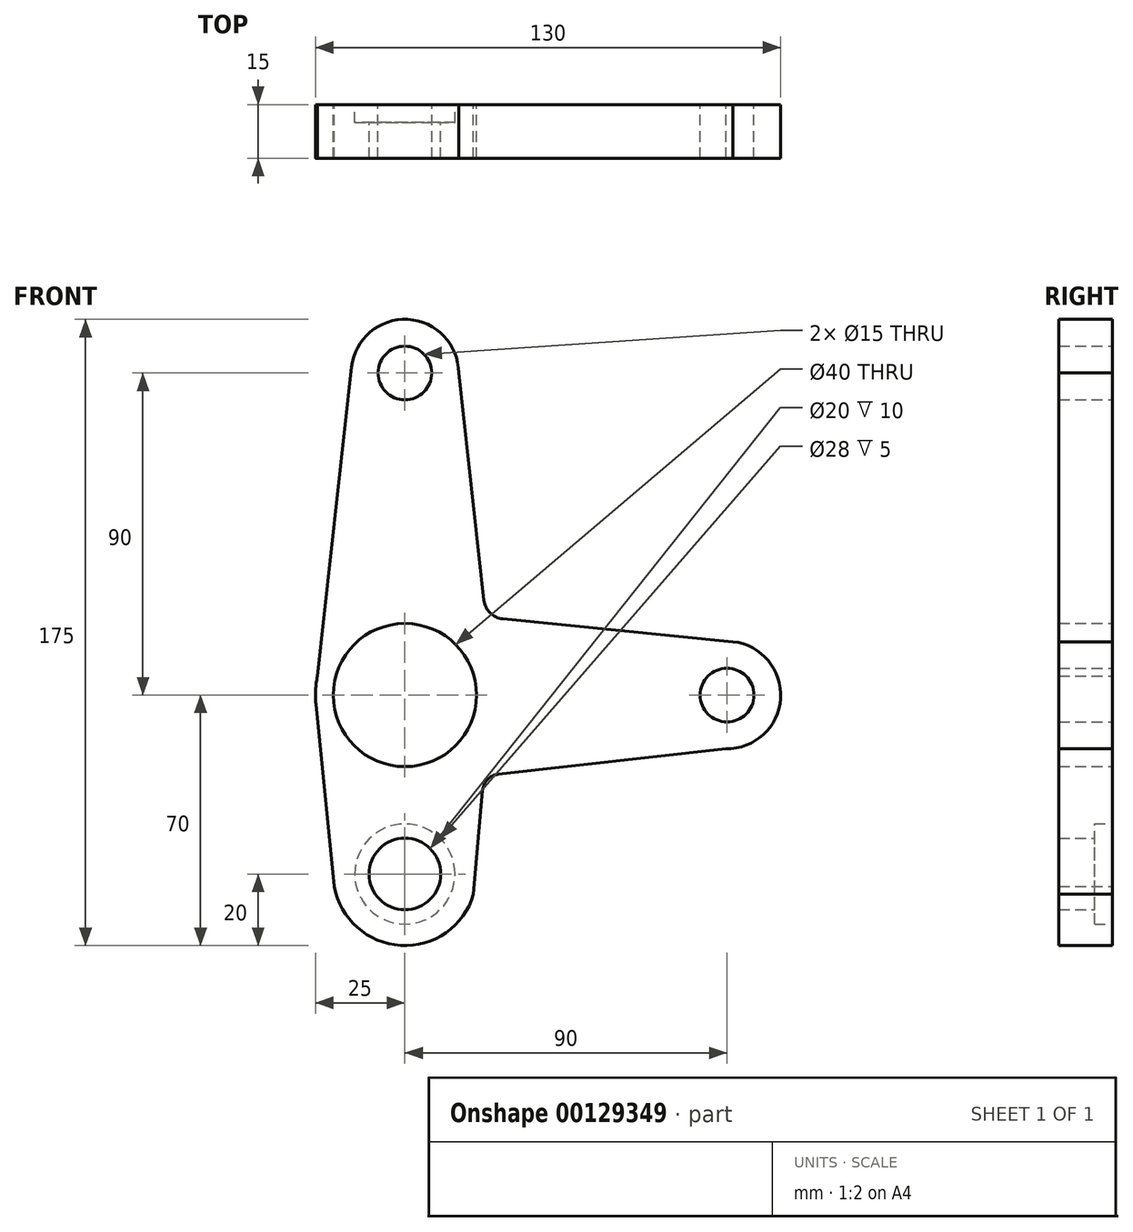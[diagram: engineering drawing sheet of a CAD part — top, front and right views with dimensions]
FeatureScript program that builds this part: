
annotation { "Feature Type Name" : "Feature", "Feature Type Description" : "" }
export const myFeature = defineFeature(function(context is Context, id is Id, definition is map)
    precondition{}
    {
        {
            var Q0;
            Q0=qCreatedBy(makeId("Front.planeOp"),FACE);
            var sketch = newSketch(context, id + "F0", { "sketchPlane" : qUnion([Q0])});
            skArc(sketch, "E0", {"start": v(-20, -0.6) * mm, "mid": v(1.44, -19.95) * mm, "end": v(19.87, 2.27) * mm});
            skCircle(sketch, "E1", {"center": v(0, 0) * mm, "radius": 10 * mm});
            skLineSegment(sketch, "E2", {"start": v(0, 0) * mm, "end": v(0, 50) * mm});
            skLineSegment(sketch, "E3", {"start": v(0, 50) * mm, "end": v(90, 50) * mm});
            skArc(sketch, "E4", {"start": v(89.67, 35) * mm, "mid": v(104.97, 49) * mm, "end": v(91.66, 64.9) * mm});
            skLineSegment(sketch, "E5", {"start": v(89.67, 35) * mm, "end": v(26.14, 27.9) * mm});
            skLineSegment(sketch, "E6", {"start": v(21.72, 23.36) * mm, "end": v(19.17, -5.69) * mm});
            skLineSegment(sketch, "E7", {"start": v(-19.7, -3.43) * mm, "end": v(-24.87, 47.47) * mm});
            skCircle(sketch, "E8", {"center": v(0, 50) * mm, "radius": 20 * mm});
            skCircle(sketch, "E9", {"center": v(90, 50) * mm, "radius": 7.5 * mm});
            skPoint(sketch, "E10.visualSharp", {"position": v(22.07, 27.44) * mm});
            skArc(sketch, "E10.filletArc", {"start": v(26.14, 27.9) * mm, "mid": v(23.12, 26.42) * mm, "end": v(21.72, 23.36) * mm});
            skLineSegment(sketch, "E11", {"start": v(0, 50) * mm, "end": v(0, 140) * mm});
            skLineSegment(sketch, "E12", {"start": v(0, 140) * mm, "end": v(42.7, 140) * mm});
            skArc(sketch, "E13", {"start": v(15, 140) * mm, "mid": v(0.82, 154.98) * mm, "end": v(-14.9, 141.64) * mm});
            skCircle(sketch, "E14", {"center": v(0, 140) * mm, "radius": 7.5 * mm});
            skLineSegment(sketch, "E15", {"start": v(-24.43, 55.31) * mm, "end": v(-14.9, 141.64) * mm});
            skLineSegment(sketch, "E16", {"start": v(22.04, 76.6) * mm, "end": v(14.91, 141.64) * mm});
            skLineSegment(sketch, "E17.trimOffspring", {"start": v(27.42, 71.28) * mm, "end": v(91.66, 64.9) * mm});
            skArc(sketch, "E18.trimOffspring", {"start": v(-24.43, 55.31) * mm, "mid": v(-24.96, 51.41) * mm, "end": v(-24.87, 47.47) * mm});
            skPoint(sketch, "E19.visualSharp", {"position": v(22.57, 71.77) * mm});
            skArc(sketch, "E19.filletArc", {"start": v(22.04, 76.6) * mm, "mid": v(23.79, 73) * mm, "end": v(27.42, 71.28) * mm});
            skSolve(sketch);
        }
        {
            var Q0;
            Q0=makeQuery(id+"F0.imprint","IMPRINT",FACE,{"disambiguationData":[TD([[makeQuery(id+"F0.imprint","IMPRINT",EDGE,{"derivedFrom":sQuery(id+"F0.wireOp",EDGE,"E1")}),-1.0]])]});
            extrude(context, id + "F1", {"entities" : qUnion([Q0]), "depth" : 15 * mm});
        }
        {
            var Q0;
            Q0=qCreatedBy(makeId("Front.planeOp"),FACE);
            var sketch = newSketch(context, id + "F2", { "sketchPlane" : qUnion([Q0])});
            skCircle(sketch, "E20", {"center": v(0, 0) * mm, "radius": 14 * mm});
            skSolve(sketch);
        }
        {
            var Q0;
            Q0=qSketchRegion(id+"F2",true);
            extrude(context, id + "F3", {"entities" : qUnion([Q0]), "operationType" : NewBodyOperationType.REMOVE, "depth" : 5 * mm});
        }
    });
